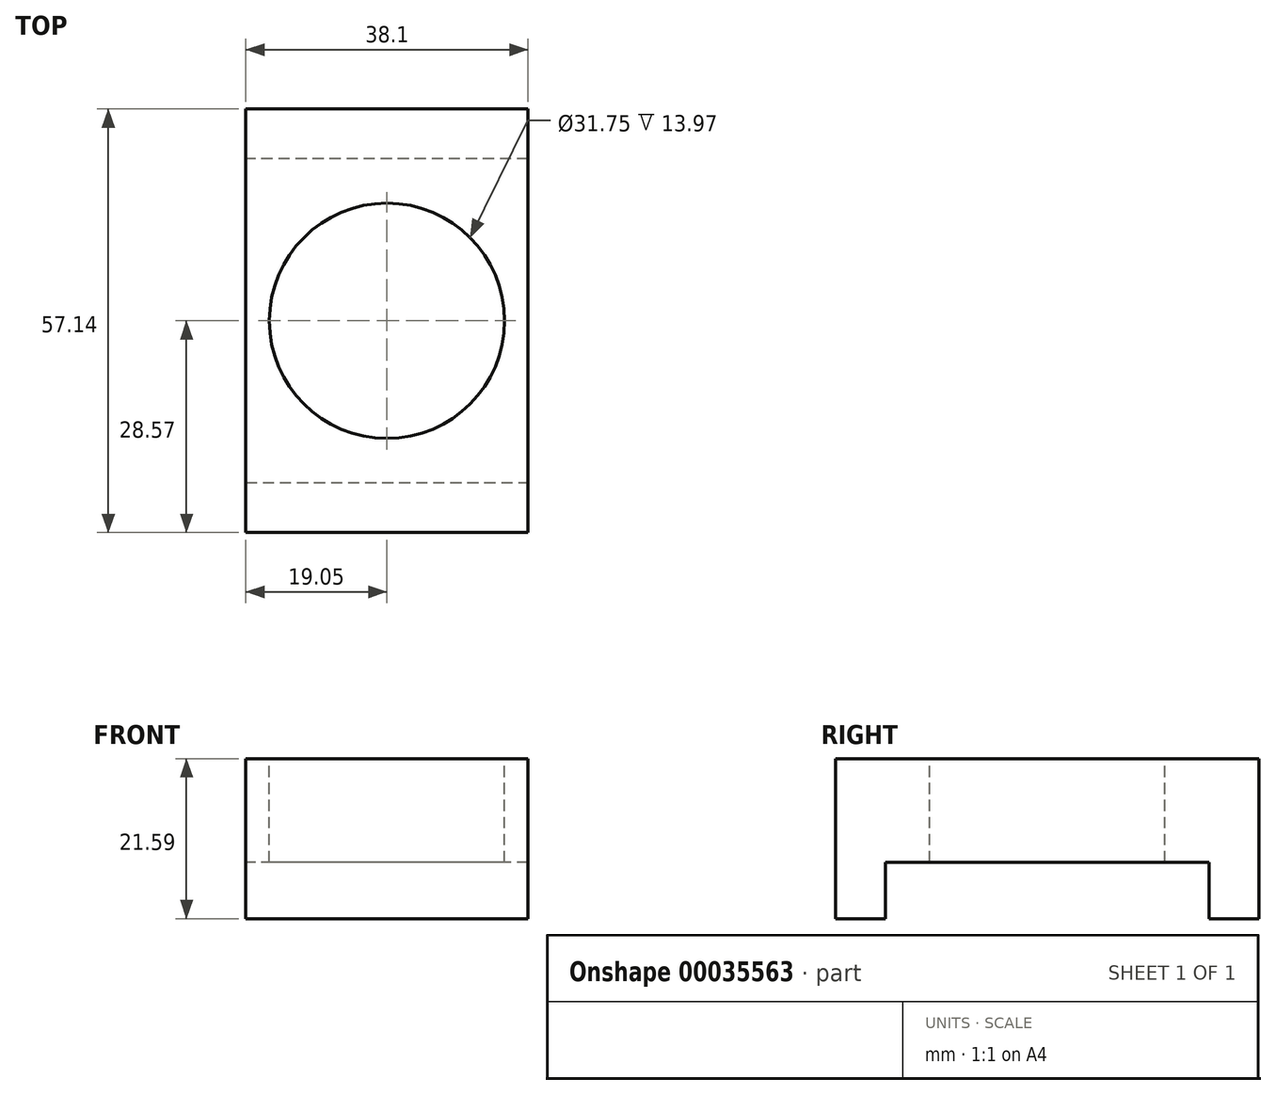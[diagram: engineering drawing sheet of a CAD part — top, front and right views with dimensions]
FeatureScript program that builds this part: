
annotation { "Feature Type Name" : "Feature", "Feature Type Description" : "" }
export const myFeature = defineFeature(function(context is Context, id is Id, definition is map)
    precondition{}
    {
        {
            var Q0;
            Q0=qCreatedBy(makeId("Top.planeOp"),FACE);
            var sketch = newSketch(context, id + "F0", { "sketchPlane" : qUnion([Q0])});
            skLineSegment(sketch, "E0.rect.bottom", {"start": v(-19.05, 28.58) * mm, "end": v(19.05, 28.58) * mm});
            skLineSegment(sketch, "E0.rect.top", {"start": v(-19.05, -28.58) * mm, "end": v(19.05, -28.58) * mm});
            skLineSegment(sketch, "E0.rect.left", {"start": v(-19.05, 28.58) * mm, "end": v(-19.05, -28.58) * mm});
            skLineSegment(sketch, "E0.rect.right", {"start": v(19.05, 28.58) * mm, "end": v(19.05, -28.58) * mm});
            skPoint(sketch, "E0.rect.middle", {"position": v(0, 0) * mm});
            skSolve(sketch);
        }
        {
            var Q0;
            Q0 = qSketchRegion(id + "F0", true);
            extrude(context, id + "F1", {"entities" : qUnion([Q0]), "depth" : 13.97 * mm});
        }
        {
            var Q0;
            Q0=makeQuery(id+"F1.opExtrude","CAP_FACE",FACE,{"disambiguationData":[OSD([sQuery(id+"F0.wireOp",EDGE,"E0.rect.bottom"),sQuery(id+"F0.wireOp",EDGE,"E0.rect.top"),sQuery(id+"F0.wireOp",EDGE,"E0.rect.left"),sQuery(id+"F0.wireOp",EDGE,"E0.rect.right")])],"isStart":false});
            var sketch = newSketch(context, id + "F2", { "sketchPlane" : qUnion([Q0])});
            skCircle(sketch, "E1", {"center": v(0, 0) * mm, "radius": 15.88 * mm});
            skSolve(sketch);
        }
        {
            var Q0;
            Q0 = qSketchRegion(id + "F2", true);
            extrude(context, id + "F3", {"entities" : qUnion([Q0]), "operationType" : NewBodyOperationType.REMOVE, "oppositeDirection" : true, "depth" : 25.4 * mm});
        }
        {
            var Q0;
            Q0=makeQuery(id+"F1.opExtrude","CAP_FACE",FACE,{"disambiguationData":[OSD([sQuery(id+"F0.wireOp",EDGE,"E0.rect.bottom"),sQuery(id+"F0.wireOp",EDGE,"E0.rect.top"),sQuery(id+"F0.wireOp",EDGE,"E0.rect.left"),sQuery(id+"F0.wireOp",EDGE,"E0.rect.right")])],"isStart":true});
            var sketch = newSketch(context, id + "F4", { "sketchPlane" : qUnion([Q0])});
            skLineSegment(sketch, "E2.bottom", {"start": v(-19.05, 28.58) * mm, "end": v(19.05, 28.58) * mm});
            skLineSegment(sketch, "E2.top", {"start": v(-19.05, 21.84) * mm, "end": v(19.05, 21.84) * mm});
            skLineSegment(sketch, "E2.left", {"start": v(-19.05, 28.58) * mm, "end": v(-19.05, 21.84) * mm});
            skLineSegment(sketch, "E2.right", {"start": v(19.05, 28.58) * mm, "end": v(19.05, 21.84) * mm});
            skLineSegment(sketch, "E3.bottom", {"start": v(19.05, -28.58) * mm, "end": v(-19.05, -28.58) * mm});
            skLineSegment(sketch, "E3.top", {"start": v(19.05, -21.84) * mm, "end": v(-19.05, -21.84) * mm});
            skLineSegment(sketch, "E3.left", {"start": v(19.05, -28.58) * mm, "end": v(19.05, -21.84) * mm});
            skLineSegment(sketch, "E3.right", {"start": v(-19.05, -28.58) * mm, "end": v(-19.05, -21.84) * mm});
            skSolve(sketch);
        }
        {
            var Q0;
            Q0 = qSketchRegion(id + "F4", true);
            extrude(context, id + "F5", {"entities" : qUnion([Q0]), "operationType" : NewBodyOperationType.ADD, "depth" : 7.62 * mm});
        }
    });
